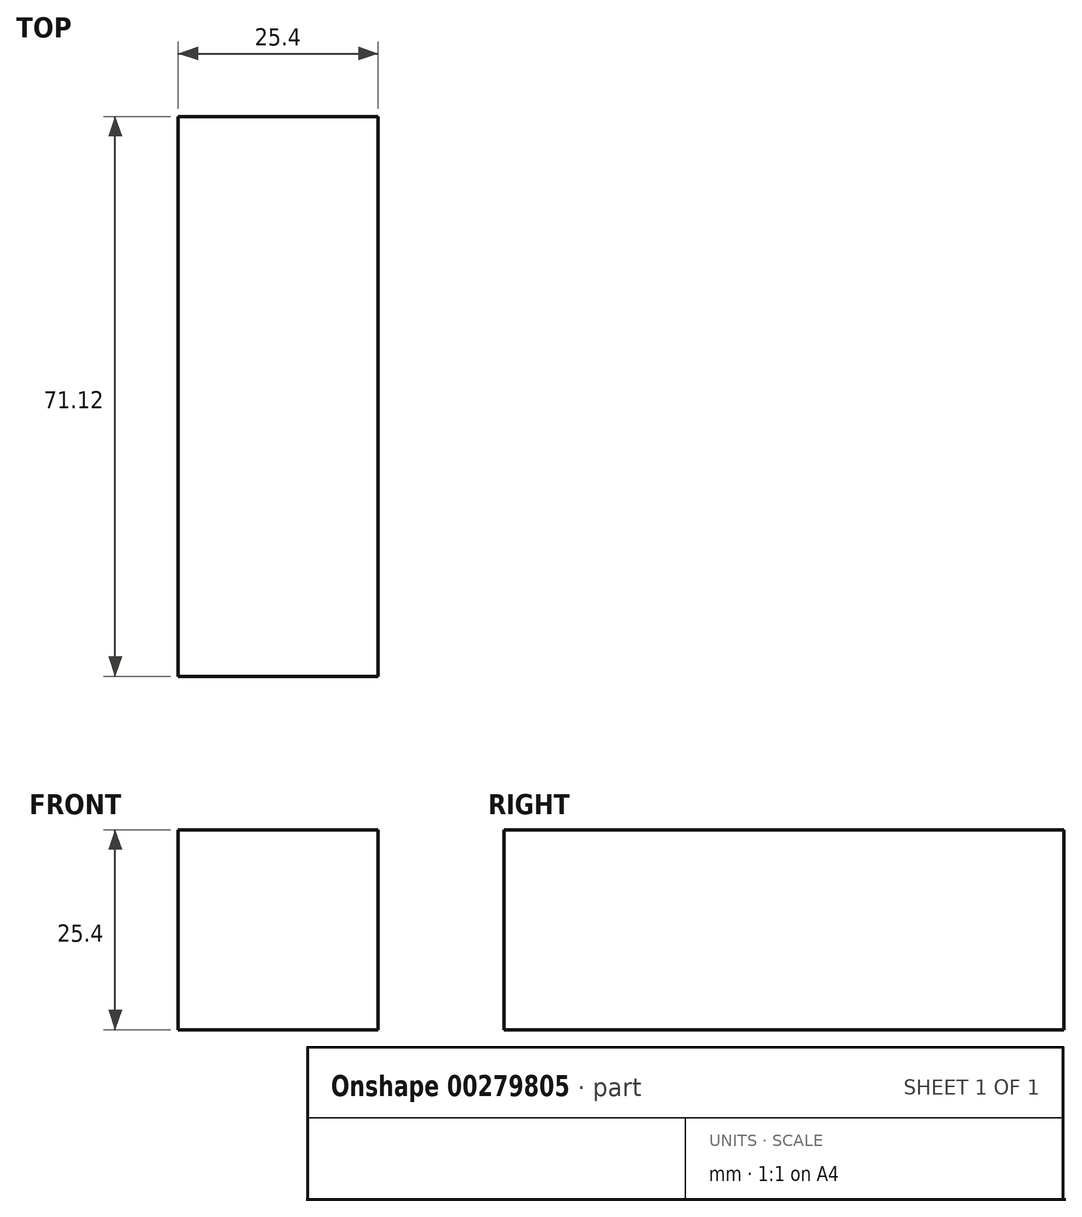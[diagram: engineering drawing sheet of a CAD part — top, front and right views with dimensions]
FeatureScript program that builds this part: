
annotation { "Feature Type Name" : "Feature", "Feature Type Description" : "" }
export const myFeature = defineFeature(function(context is Context, id is Id, definition is map)
    precondition{}
    {
        {
            var Q0;
            Q0=qCreatedBy(makeId("Front.planeOp"),FACE);
            var sketch = newSketch(context, id + "F0", { "sketchPlane" : qUnion([Q0])});
            skLineSegment(sketch, "E0.bottom", {"start": v(-8.6, -13.5) * mm, "end": v(-34, -13.5) * mm});
            skLineSegment(sketch, "E0.top", {"start": v(-8.6, -38.9) * mm, "end": v(-34, -38.9) * mm});
            skLineSegment(sketch, "E0.left", {"start": v(-8.6, -13.5) * mm, "end": v(-8.6, -38.9) * mm});
            skLineSegment(sketch, "E0.right", {"start": v(-34, -13.5) * mm, "end": v(-34, -38.9) * mm});
            skSolve(sketch);
        }
        {
            var Q0;
            Q0=makeQuery(id+"F0.imprint","IMPRINT",FACE,{"disambiguationData":[TD([[makeQuery(id+"F0.imprint","IMPRINT",EDGE,{"derivedFrom":sQuery(id+"F0.wireOp",EDGE,"E0.bottom")}),1.0]])]});
            extrude(context, id + "F1", {"entities" : qUnion([Q0]), "depth" : 71.12 * mm});
        }
    });
